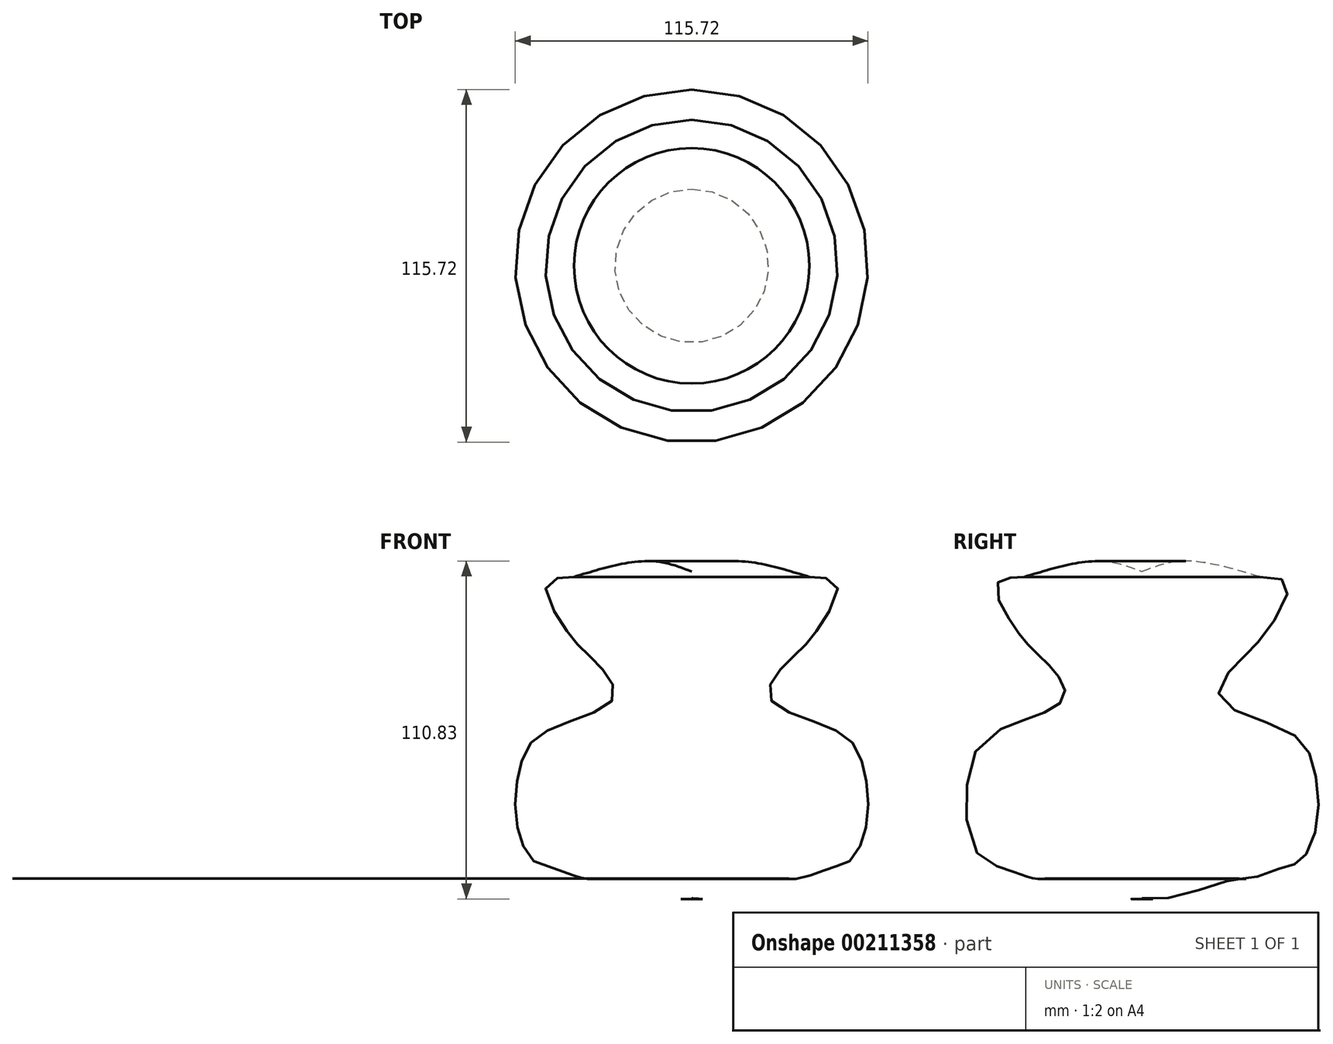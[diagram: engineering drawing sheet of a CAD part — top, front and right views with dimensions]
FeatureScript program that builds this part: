
annotation { "Feature Type Name" : "Feature", "Feature Type Description" : "" }
export const myFeature = defineFeature(function(context is Context, id is Id, definition is map)
    precondition{}
    {
        {
            var Q0;
            Q0=qCreatedBy(makeId("Right.planeOp"),FACE);
            var sketch = newSketch(context, id + "F0", { "sketchPlane" : qUnion([Q0])});
            skFitSpline(sketch, "E0", {"points": [v(38.6, 48.59) * mm, v(47.78, 45.86) * mm, v(39.34, 28.74) * mm, v(32.15, 21.3) * mm, v(25.45, 9.14) * mm, v(47.78, -2.02) * mm, v(56.21, -13.19) * mm, v(57.2, -33.53) * mm, v(51.75, -44.7) * mm, v(46.3, -46.68) * mm, v(35.13, -50.4) * mm, v(30.9, -50.4) * mm, v(10.56, -56.36) * mm, v(-5.81, -55.86) * mm, v(-9.53, -55.12) * mm, v(-8.79, -55.86) * mm, v(-12.76, -54.62) * mm, v(-12.76, -54.37) * mm], "startDerivative": vector(217.18, -3.14) * mm, "endDerivative": vector(18.24, 22.67) * mm});
            skFitSpline(sketch, "E1", {"points": [v(38.6, 48.59) * mm, v(10.56, 53.55) * mm, v(-6.3, 48.59) * mm, v(-17.72, 51.07) * mm], "startDerivative": vector(-72.05, 22.22) * mm, "endDerivative": vector(-41.96, 16.75) * mm});
            skLineSegment(sketch, "E2", {"start": v(0, 63.47) * mm, "end": v(0, -69.75) * mm});
            skSolve(sketch);
        }
        {
            var Q0;
            Q0 = qSketchRegion(id + "F0", true);
            var Q1;
            Q1=sQuery(id+"F0.wireOp",EDGE,"E2");
            revolve(context, id + "F1", {"entities" : qUnion([Q0]), "axis" : qUnion([Q1]), "revolveType" : RevolveType.FULL});
        }
    });
